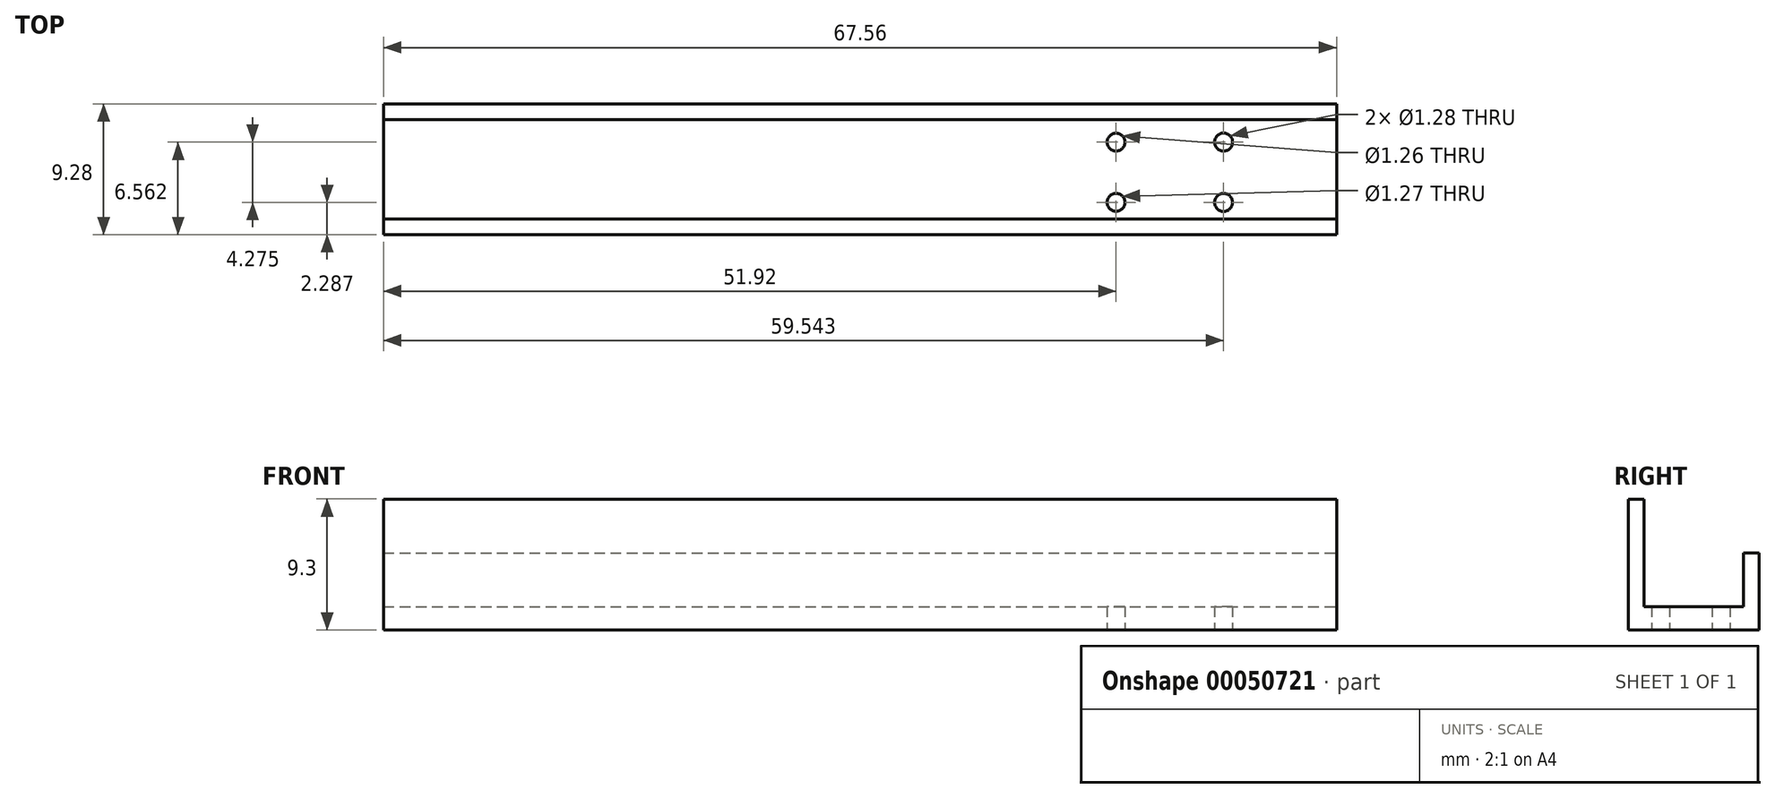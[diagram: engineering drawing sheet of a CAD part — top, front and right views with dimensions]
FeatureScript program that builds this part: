
annotation { "Feature Type Name" : "Feature", "Feature Type Description" : "" }
export const myFeature = defineFeature(function(context is Context, id is Id, definition is map)
    precondition{}
    {
        {
            var Q0;
            Q0=qCreatedBy(makeId("Top.planeOp"),FACE);
            var sketch = newSketch(context, id + "F0", { "sketchPlane" : qUnion([Q0])});
            skLineSegment(sketch, "E0", {"start": v(-33.66, 4.64) * mm, "end": v(-33.66, -4.64) * mm});
            skLineSegment(sketch, "E1", {"start": v(-33.66, -4.64) * mm, "end": v(33.9, -4.64) * mm});
            skLineSegment(sketch, "E2", {"start": v(33.9, -4.64) * mm, "end": v(33.9, 4.64) * mm});
            skLineSegment(sketch, "E3", {"start": v(-33.66, 4.64) * mm, "end": v(33.9, 4.64) * mm});
            skSolve(sketch);
        }
        {
            var Q0;
            Q0=makeQuery(id+"F0.imprint","IMPRINT",FACE,{"disambiguationData":[TD([[makeQuery(id+"F0.imprint","IMPRINT",EDGE,{"derivedFrom":sQuery(id+"F0.wireOp",EDGE,"E0")}),1.0]])]});
            extrude(context, id + "F1", {"entities" : qUnion([Q0]), "depth" : 1.68 * mm});
        }
        {
            var Q0;
            Q0=makeQuery(id+"F1.opExtrude","CAP_FACE",FACE,{"disambiguationData":[OSD([sQuery(id+"F0.wireOp",EDGE,"E0"),sQuery(id+"F0.wireOp",EDGE,"E1"),sQuery(id+"F0.wireOp",EDGE,"E2"),sQuery(id+"F0.wireOp",EDGE,"E3")])],"isStart":false});
            var sketch = newSketch(context, id + "F2", { "sketchPlane" : qUnion([Q0])});
            skLineSegment(sketch, "E4", {"start": v(-33.66, -4.64) * mm, "end": v(-33.66, -3.52) * mm});
            skLineSegment(sketch, "E5", {"start": v(-33.66, -3.52) * mm, "end": v(33.9, -3.52) * mm});
            skLineSegment(sketch, "E6", {"start": v(33.9, -3.52) * mm, "end": v(33.9, -4.64) * mm});
            skLineSegment(sketch, "E7", {"start": v(33.9, -4.64) * mm, "end": v(-33.66, -4.64) * mm});
            skLineSegment(sketch, "E8", {"start": v(-33.66, 4.64) * mm, "end": v(-33.66, 3.5) * mm});
            skLineSegment(sketch, "E9", {"start": v(-33.66, 3.5) * mm, "end": v(33.9, 3.5) * mm});
            skLineSegment(sketch, "E10", {"start": v(33.9, 3.5) * mm, "end": v(33.9, 4.64) * mm});
            skLineSegment(sketch, "E11", {"start": v(33.9, 4.64) * mm, "end": v(-33.66, 4.64) * mm});
            skSolve(sketch);
        }
        {
            var Q0;
            Q0=makeQuery(id+"F2.imprint","IMPRINT",FACE,{"disambiguationData":[TD([[makeQuery(id+"F2.imprint","IMPRINT",EDGE,{"derivedFrom":sQuery(id+"F2.wireOp",EDGE,"E4")}),1.0]])]});
            extrude(context, id + "F3", {"entities" : qUnion([Q0]), "operationType" : NewBodyOperationType.ADD, "depth" : 7.62 * mm});
        }
        {
            var Q0;
            Q0=makeQuery(id+"F2.imprint","IMPRINT",FACE,{"disambiguationData":[TD([[makeQuery(id+"F2.imprint","IMPRINT",EDGE,{"derivedFrom":sQuery(id+"F2.wireOp",EDGE,"E8")}),1.0]])]});
            extrude(context, id + "F4", {"entities" : qUnion([Q0]), "operationType" : NewBodyOperationType.ADD, "depth" : 3.8 * mm});
        }
        {
            var Q0;
            Q0=makeQuery(id+"F1.opExtrude","CAP_FACE",FACE,{"disambiguationData":[OSD([sQuery(id+"F0.wireOp",EDGE,"E0"),sQuery(id+"F0.wireOp",EDGE,"E1"),sQuery(id+"F0.wireOp",EDGE,"E2"),sQuery(id+"F0.wireOp",EDGE,"E3")])],"isStart":true});
            var sketch = newSketch(context, id + "F5", { "sketchPlane" : qUnion([Q0])});
            skLineSegment(sketch, "E12", {"start": v(33.9, 4.64) * mm, "end": v(33.9, 2.35) * mm});
            skLineSegment(sketch, "E13", {"start": v(33.9, -4.64) * mm, "end": v(33.9, -1.92) * mm});
            skCircle(sketch, "E14", {"center": v(25.9, 2.35) * mm, "radius": 0.64 * mm});
            skCircle(sketch, "E15", {"center": v(25.9, -1.92) * mm, "radius": 0.64 * mm});
            skCircle(sketch, "E16", {"center": v(18.27, 2.35) * mm, "radius": 0.63 * mm});
            skCircle(sketch, "E17", {"center": v(18.27, -1.92) * mm, "radius": 0.63 * mm});
            skSolve(sketch);
        }
        {
            var Q0;
            Q0 = qSketchRegion(id + "F5", true);
            extrude(context, id + "F6", {"entities" : qUnion([Q0]), "operationType" : NewBodyOperationType.REMOVE, "oppositeDirection" : true, "depth" : 25.4 * mm});
        }
    });
